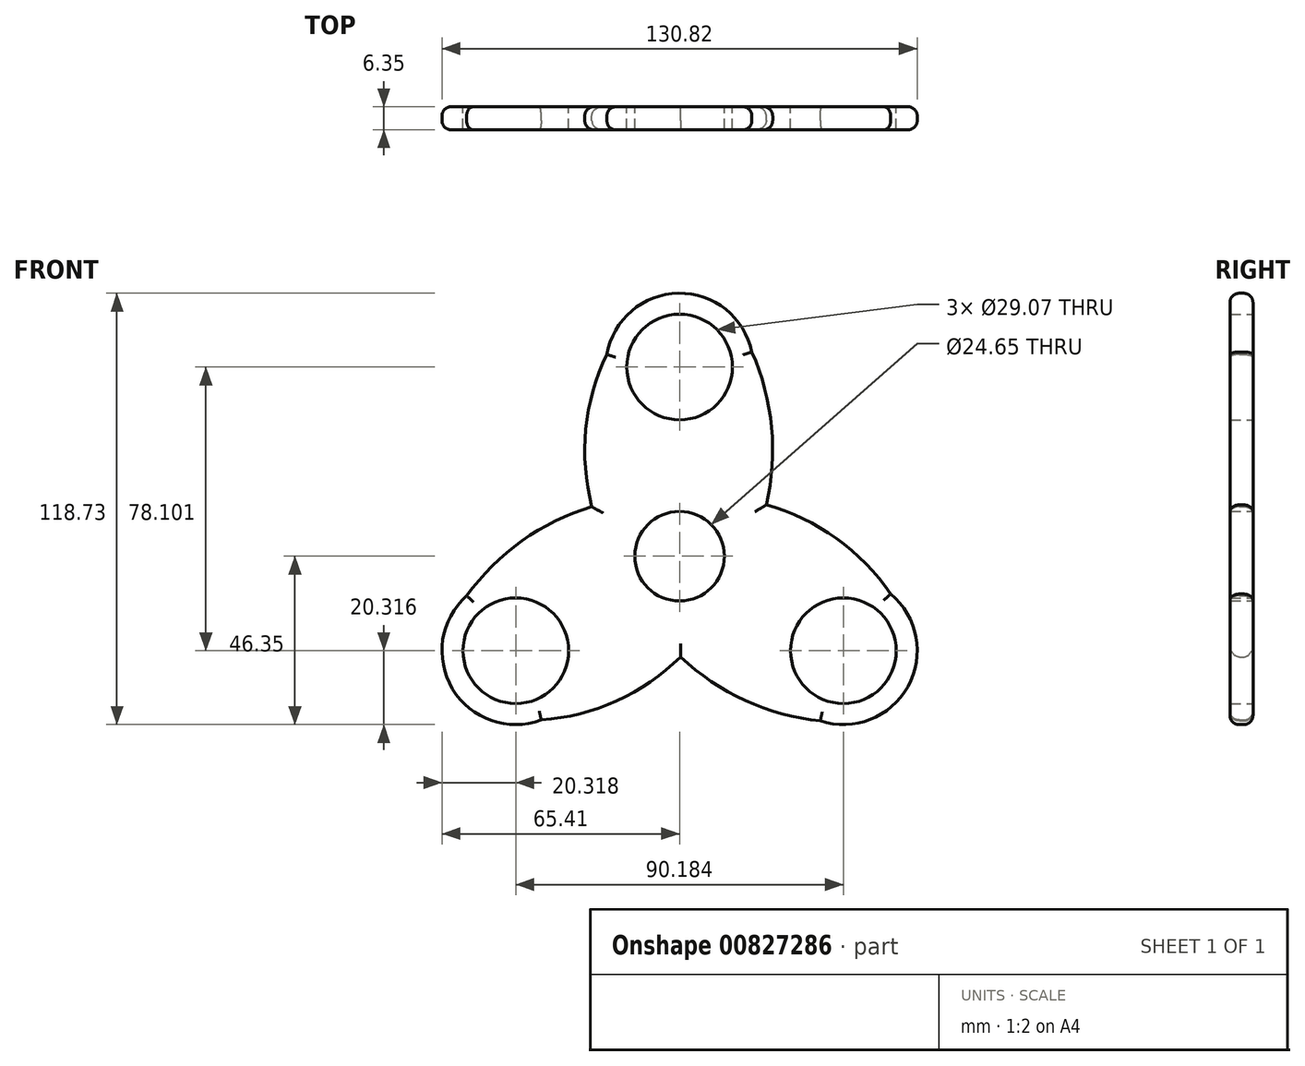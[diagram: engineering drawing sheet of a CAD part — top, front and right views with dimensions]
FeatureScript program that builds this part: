
annotation { "Feature Type Name" : "Feature", "Feature Type Description" : "" }
export const myFeature = defineFeature(function(context is Context, id is Id, definition is map)
    precondition{}
    {
        {
            var Q0;
            Q0=qCreatedBy(makeId("Front.planeOp"),FACE);
            var sketch = newSketch(context, id + "F0", { "sketchPlane" : qUnion([Q0])});
            skCircle(sketch, "E0", {"center": v(0, 0) * mm, "radius": 12.32 * mm});
            skCircle(sketch, "E1", {"center": v(0, 52.07) * mm, "radius": 14.53 * mm});
            skArc(sketch, "E2", {"start": v(19.9, 56.2) * mm, "mid": v(-0.34, 72.38) * mm, "end": v(-20.02, 55.53) * mm});
            skArc(sketch, "E3", {"start": v(23.88, 14.11) * mm, "mid": v(25.33, 35.49) * mm, "end": v(19.9, 56.2) * mm});
            skArc(sketch, "E4", {"start": v(-20.02, 55.53) * mm, "mid": v(-25.81, 34.95) * mm, "end": v(-24.16, 13.62) * mm});
            skArc(sketch, "E5.1.0", {"start": v(-24.16, 13.62) * mm, "mid": v(-43.4, 4.2) * mm, "end": v(-58.62, -10.88) * mm});
            skArc(sketch, "E5.1.1", {"start": v(-58.62, -10.88) * mm, "mid": v(-62.51, -36.49) * mm, "end": v(-38.08, -45.1) * mm});
            skArc(sketch, "E5.1.2", {"start": v(-38.08, -45.1) * mm, "mid": v(-17.36, -39.83) * mm, "end": v(0.28, -27.74) * mm});
            skCircle(sketch, "E5.1.3", {"center": v(-45.1, -26.03) * mm, "radius": 14.53 * mm});
            skArc(sketch, "E5.2.0", {"start": v(0.28, -27.74) * mm, "mid": v(18.07, -39.68) * mm, "end": v(38.73, -45.33) * mm});
            skArc(sketch, "E5.2.1", {"start": v(38.73, -45.33) * mm, "mid": v(62.86, -35.9) * mm, "end": v(58.1, -10.43) * mm});
            skArc(sketch, "E5.2.2", {"start": v(58.1, -10.43) * mm, "mid": v(43.17, 4.88) * mm, "end": v(23.88, 14.11) * mm});
            skCircle(sketch, "E5.2.3", {"center": v(45.1, -26.03) * mm, "radius": 14.53 * mm});
            skPoint(sketch, "E6.orphan", {"position": v(-9.42, 16.3) * mm});
            skPoint(sketch, "E7.orphan", {"position": v(9.42, 16.3) * mm});
            skPoint(sketch, "E8.orphan", {"position": v(18.83, 0) * mm});
            skPoint(sketch, "E9.orphan", {"position": v(9.42, -16.3) * mm});
            skPoint(sketch, "E10.orphan", {"position": v(-9.42, -16.3) * mm});
            skPoint(sketch, "E11.orphan", {"position": v(-18.83, 0) * mm});
            skSolve(sketch);
        }
        {
            var Q0;
            Q0=makeQuery(id+"F0.imprint","IMPRINT",FACE,{"disambiguationData":[TD([[makeQuery(id+"F0.imprint","IMPRINT",EDGE,{"derivedFrom":sQuery(id+"F0.wireOp",EDGE,"E0")}),-1.0]])]});
            extrude(context, id + "F1", {"entities" : qUnion([Q0]), "depth" : 6.35 * mm, "offsetDistance" : 25.4 * mm});
        }
        {
            var Q0;
            Q0=makeQuery(id+"F1.opExtrude","CAP_EDGE",EDGE,{"disambiguationData":[OSD([sQuery(id+"F0.wireOp",EDGE,"E5.1.1")])],"isStart":false});
            var Q1;
            Q1=makeQuery(id+"F1.opExtrude","CAP_EDGE",EDGE,{"disambiguationData":[OSD([sQuery(id+"F0.wireOp",EDGE,"E5.1.2")])],"isStart":false});
            var Q2;
            Q2=makeQuery(id+"F1.opExtrude","CAP_EDGE",EDGE,{"disambiguationData":[OSD([sQuery(id+"F0.wireOp",EDGE,"E5.2.0")])],"isStart":false});
            var Q3;
            Q3=makeQuery(id+"F1.opExtrude","CAP_EDGE",EDGE,{"disambiguationData":[OSD([sQuery(id+"F0.wireOp",EDGE,"E5.1.0")])],"isStart":false});
            var Q4;
            Q4=makeQuery(id+"F1.opExtrude","CAP_EDGE",EDGE,{"disambiguationData":[OSD([sQuery(id+"F0.wireOp",EDGE,"E4")])],"isStart":false});
            var Q5;
            Q5=makeQuery(id+"F1.opExtrude","CAP_EDGE",EDGE,{"disambiguationData":[OSD([sQuery(id+"F0.wireOp",EDGE,"E2")])],"isStart":false});
            var Q6;
            Q6=makeQuery(id+"F1.opExtrude","CAP_EDGE",EDGE,{"disambiguationData":[OSD([sQuery(id+"F0.wireOp",EDGE,"E3")])],"isStart":false});
            var Q7;
            Q7=makeQuery(id+"F1.opExtrude","CAP_EDGE",EDGE,{"disambiguationData":[OSD([sQuery(id+"F0.wireOp",EDGE,"E5.2.2")])],"isStart":false});
            var Q8;
            Q8=makeQuery(id+"F1.opExtrude","CAP_EDGE",EDGE,{"disambiguationData":[OSD([sQuery(id+"F0.wireOp",EDGE,"E5.2.1")])],"isStart":false});
            fillet(context, id + "F2", {"entities" : qUnion([Q0, Q1, Q2, Q3, Q4, Q5, Q6, Q7, Q8]), "radius" : 2.54 * mm, "tangentPropagation" : true, "allowEdgeOverflow" : false});
        }
        {
            var Q0;
            Q0=makeQuery(id+"F1.opExtrude","CAP_EDGE",EDGE,{"disambiguationData":[OSD([sQuery(id+"F0.wireOp",EDGE,"E3")])],"isStart":true});
            var Q1;
            Q1=makeQuery(id+"F1.opExtrude","CAP_EDGE",EDGE,{"disambiguationData":[OSD([sQuery(id+"F0.wireOp",EDGE,"E2")])],"isStart":true});
            var Q2;
            Q2=makeQuery(id+"F1.opExtrude","CAP_EDGE",EDGE,{"disambiguationData":[OSD([sQuery(id+"F0.wireOp",EDGE,"E4")])],"isStart":true});
            var Q3;
            Q3=makeQuery(id+"F1.opExtrude","CAP_EDGE",EDGE,{"disambiguationData":[OSD([sQuery(id+"F0.wireOp",EDGE,"E5.1.0")])],"isStart":true});
            var Q4;
            Q4=makeQuery(id+"F1.opExtrude","CAP_EDGE",EDGE,{"disambiguationData":[OSD([sQuery(id+"F0.wireOp",EDGE,"E5.1.1")])],"isStart":true});
            var Q5;
            Q5=makeQuery(id+"F1.opExtrude","CAP_EDGE",EDGE,{"disambiguationData":[OSD([sQuery(id+"F0.wireOp",EDGE,"E5.1.2")])],"isStart":true});
            var Q6;
            Q6=makeQuery(id+"F1.opExtrude","CAP_EDGE",EDGE,{"disambiguationData":[OSD([sQuery(id+"F0.wireOp",EDGE,"E5.2.0")])],"isStart":true});
            var Q7;
            Q7=makeQuery(id+"F1.opExtrude","CAP_EDGE",EDGE,{"disambiguationData":[OSD([sQuery(id+"F0.wireOp",EDGE,"E5.2.1")])],"isStart":true});
            var Q8;
            Q8=makeQuery(id+"F1.opExtrude","CAP_EDGE",EDGE,{"disambiguationData":[OSD([sQuery(id+"F0.wireOp",EDGE,"E5.2.2")])],"isStart":true});
            fillet(context, id + "F3", {"entities" : qUnion([Q0, Q1, Q2, Q3, Q4, Q5, Q6, Q7, Q8]), "radius" : 2.54 * mm, "tangentPropagation" : true, "allowEdgeOverflow" : false});
        }
    });
